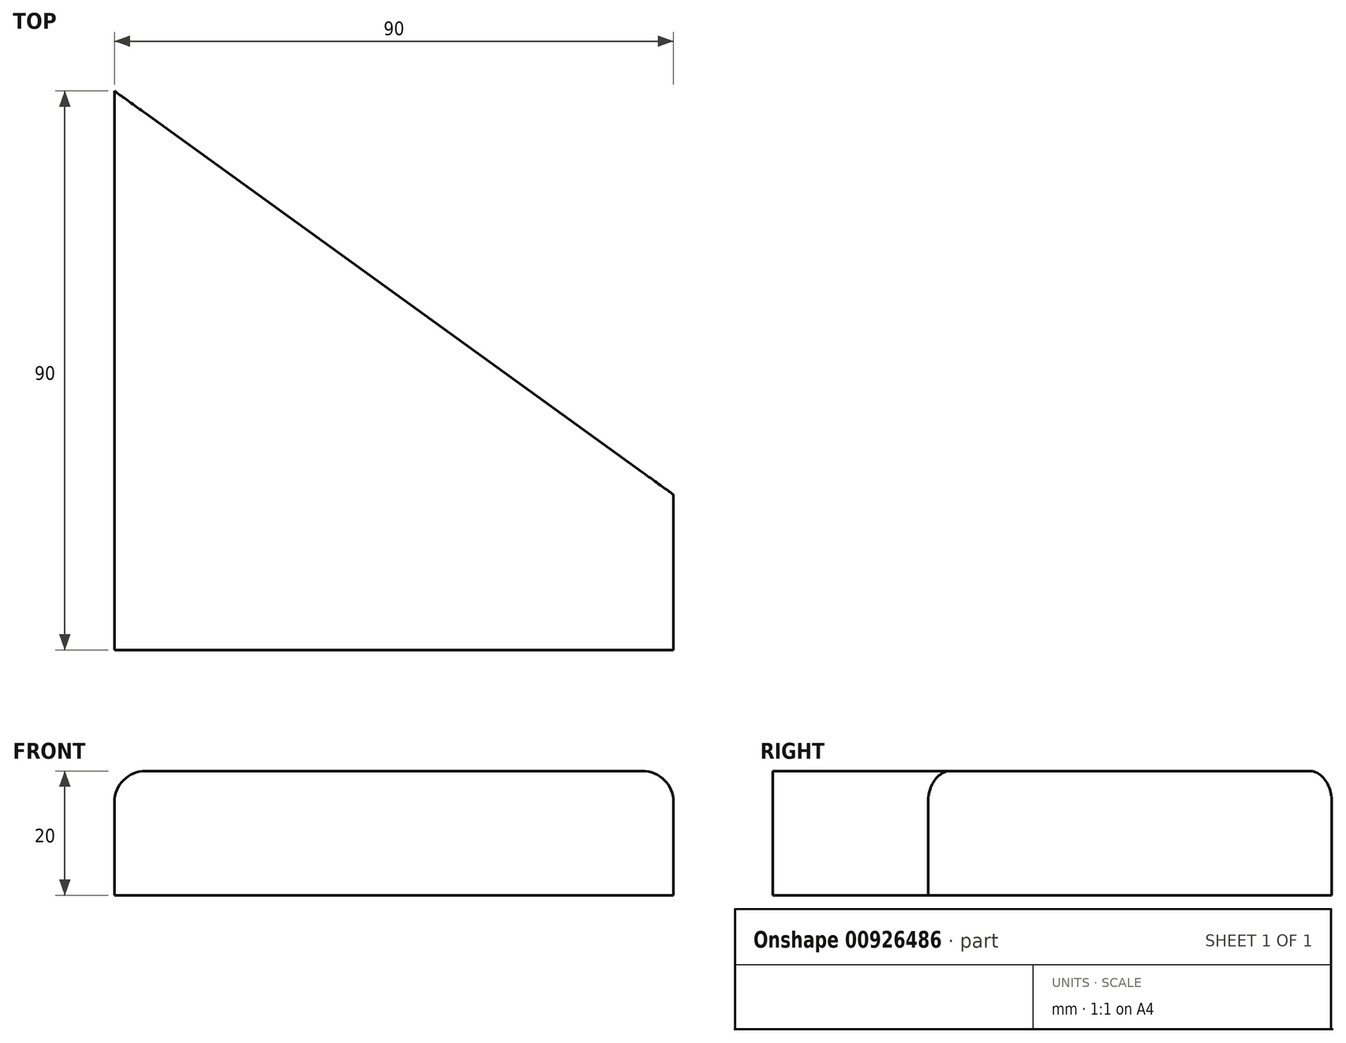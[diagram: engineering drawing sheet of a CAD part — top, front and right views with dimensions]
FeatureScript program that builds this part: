
annotation { "Feature Type Name" : "Feature", "Feature Type Description" : "" }
export const myFeature = defineFeature(function(context is Context, id is Id, definition is map)
    precondition{}
    {
        {
            var Q0;
            Q0=qCreatedBy(makeId("Top.planeOp"),FACE);
            var sketch = newSketch(context, id + "F0", { "sketchPlane" : qUnion([Q0])});
            skLineSegment(sketch, "E0", {"start": v(0, 0) * mm, "end": v(90, 0) * mm});
            skLineSegment(sketch, "E1", {"start": v(90, 0) * mm, "end": v(90, 25) * mm});
            skLineSegment(sketch, "E2", {"start": v(0, 90) * mm, "end": v(0, 0) * mm});
            skLineSegment(sketch, "E3", {"start": v(90, 25) * mm, "end": v(0, 90) * mm});
            skSolve(sketch);
        }
        {
            var Q0;
            Q0=qCreatedBy(makeId("Front.planeOp"),FACE);
            var sketch = newSketch(context, id + "F1", { "sketchPlane" : qUnion([Q0])});
            skLineSegment(sketch, "E4.bottom", {"start": v(0, 0) * mm, "end": v(90, 0) * mm});
            skLineSegment(sketch, "E4.top", {"start": v(5, 20) * mm, "end": v(85, 20) * mm});
            skLineSegment(sketch, "E4.left", {"start": v(0, 0) * mm, "end": v(0, 15) * mm});
            skLineSegment(sketch, "E4.right", {"start": v(90, 0) * mm, "end": v(90, 15) * mm});
            skPoint(sketch, "E5.visualSharp", {"position": v(0, 20) * mm});
            skArc(sketch, "E5.filletArc", {"start": v(5, 20) * mm, "mid": v(1.46, 18.54) * mm, "end": v(0, 15) * mm});
            skPoint(sketch, "E6.visualSharp", {"position": v(90, 20) * mm});
            skArc(sketch, "E6.filletArc", {"start": v(90, 15) * mm, "mid": v(88.54, 18.54) * mm, "end": v(85, 20) * mm});
            skSolve(sketch);
        }
        {
            var Q0;
            Q0=makeQuery(id+"F0.imprint","IMPRINT",FACE,{"disambiguationData":[TD([[makeQuery(id+"F0.imprint","IMPRINT",EDGE,{"derivedFrom":sQuery(id+"F0.wireOp",EDGE,"E0")}),1.0]])]});
            extrude(context, id + "F2", {"entities" : qUnion([Q0]), "depth" : 20 * mm, "offsetDistance" : 25 * mm});
        }
        {
            var Q0;
            Q0 = qSketchRegion(id + "F1", true);
            extrude(context, id + "F3", {"entities" : qUnion([Q0]), "operationType" : NewBodyOperationType.INTERSECT, "endBound" : BoundingType.UP_TO_NEXT, "oppositeDirection" : true, "depth" : 25 * mm, "offsetDistance" : 25 * mm});
        }
    });
